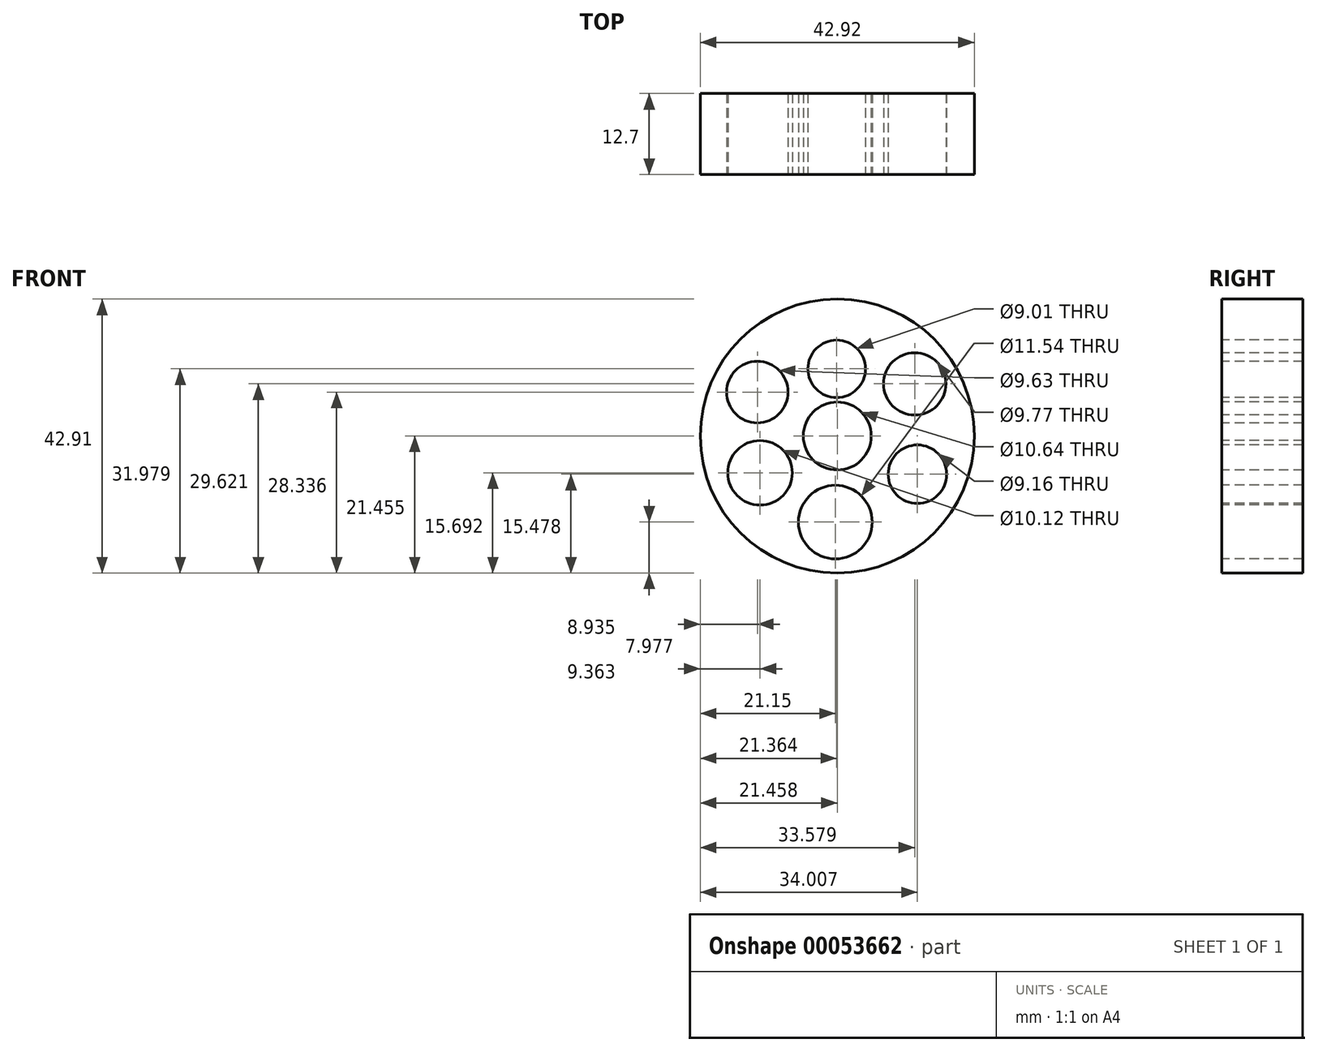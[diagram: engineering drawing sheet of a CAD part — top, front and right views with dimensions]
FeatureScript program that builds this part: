
annotation { "Feature Type Name" : "Feature", "Feature Type Description" : "" }
export const myFeature = defineFeature(function(context is Context, id is Id, definition is map)
    precondition{}
    {
        {
            var Q0;
            Q0=qCreatedBy(makeId("Front.planeOp"),FACE);
            var sketch = newSketch(context, id + "F0", { "sketchPlane" : qUnion([Q0])});
            skCircle(sketch, "E0", {"center": v(-1.8, 22.35) * mm, "radius": 21.46 * mm});
            skSolve(sketch);
        }
        {
            var Q0;
            Q0=makeQuery(id+"F0.imprint","IMPRINT",FACE,{"disambiguationData":[TD([[makeQuery(id+"F0.imprint","IMPRINT",EDGE,{"derivedFrom":sQuery(id+"F0.wireOp",EDGE,"E0")}),1.0]])]});
            extrude(context, id + "F1", {"entities" : qUnion([Q0]), "depth" : 12.7 * mm});
        }
        {
            var Q0;
            Q0=makeQuery(id+"F1.opExtrude","CAP_FACE",FACE,{"disambiguationData":[OSD([sQuery(id+"F0.wireOp",EDGE,"E0")])],"isStart":false});
            var sketch = newSketch(context, id + "F2", { "sketchPlane" : qUnion([Q0])});
            skCircle(sketch, "E1", {"center": v(-1.8, 22.35) * mm, "radius": 5.32 * mm});
            skCircle(sketch, "E2", {"center": v(-14.33, 29.23) * mm, "radius": 4.82 * mm});
            skCircle(sketch, "E3", {"center": v(-1.9, 32.87) * mm, "radius": 4.5 * mm});
            skCircle(sketch, "E4", {"center": v(10.32, 30.51) * mm, "radius": 4.89 * mm});
            skCircle(sketch, "E5", {"center": v(-13.9, 16.58) * mm, "radius": 5.06 * mm});
            skCircle(sketch, "E6", {"center": v(-2.11, 8.87) * mm, "radius": 5.77 * mm});
            skCircle(sketch, "E7", {"center": v(10.75, 16.37) * mm, "radius": 4.58 * mm});
            skSolve(sketch);
        }
        {
            var Q0;
            Q0=makeQuery(id+"F2.imprint","IMPRINT",FACE,{"disambiguationData":[TD([[makeQuery(id+"F2.imprint","IMPRINT",EDGE,{"derivedFrom":sQuery(id+"F2.wireOp",EDGE,"E3")}),1.0]])]});
            var Q1;
            Q1=makeQuery(id+"F2.imprint","IMPRINT",FACE,{"disambiguationData":[TD([[makeQuery(id+"F2.imprint","IMPRINT",EDGE,{"derivedFrom":sQuery(id+"F2.wireOp",EDGE,"E4")}),1.0]])]});
            var Q2;
            Q2=makeQuery(id+"F2.imprint","IMPRINT",FACE,{"disambiguationData":[TD([[makeQuery(id+"F2.imprint","IMPRINT",EDGE,{"derivedFrom":sQuery(id+"F2.wireOp",EDGE,"E1")}),1.0]])]});
            var Q3;
            Q3=makeQuery(id+"F2.imprint","IMPRINT",FACE,{"disambiguationData":[TD([[makeQuery(id+"F2.imprint","IMPRINT",EDGE,{"derivedFrom":sQuery(id+"F2.wireOp",EDGE,"E7")}),1.0]])]});
            var Q4;
            Q4=makeQuery(id+"F2.imprint","IMPRINT",FACE,{"disambiguationData":[TD([[makeQuery(id+"F2.imprint","IMPRINT",EDGE,{"derivedFrom":sQuery(id+"F2.wireOp",EDGE,"E5")}),1.0]])]});
            var Q5;
            Q5=makeQuery(id+"F2.imprint","IMPRINT",FACE,{"disambiguationData":[TD([[makeQuery(id+"F2.imprint","IMPRINT",EDGE,{"derivedFrom":sQuery(id+"F2.wireOp",EDGE,"E2")}),1.0]])]});
            var Q6;
            Q6=makeQuery(id+"F2.imprint","IMPRINT",FACE,{"disambiguationData":[TD([[makeQuery(id+"F2.imprint","IMPRINT",EDGE,{"derivedFrom":sQuery(id+"F2.wireOp",EDGE,"E6")}),1.0]])]});
            extrude(context, id + "F3", {"entities" : qUnion([Q0, Q1, Q2, Q3, Q4, Q5, Q6]), "operationType" : NewBodyOperationType.REMOVE, "oppositeDirection" : true, "depth" : 25.4 * mm});
        }
    });
